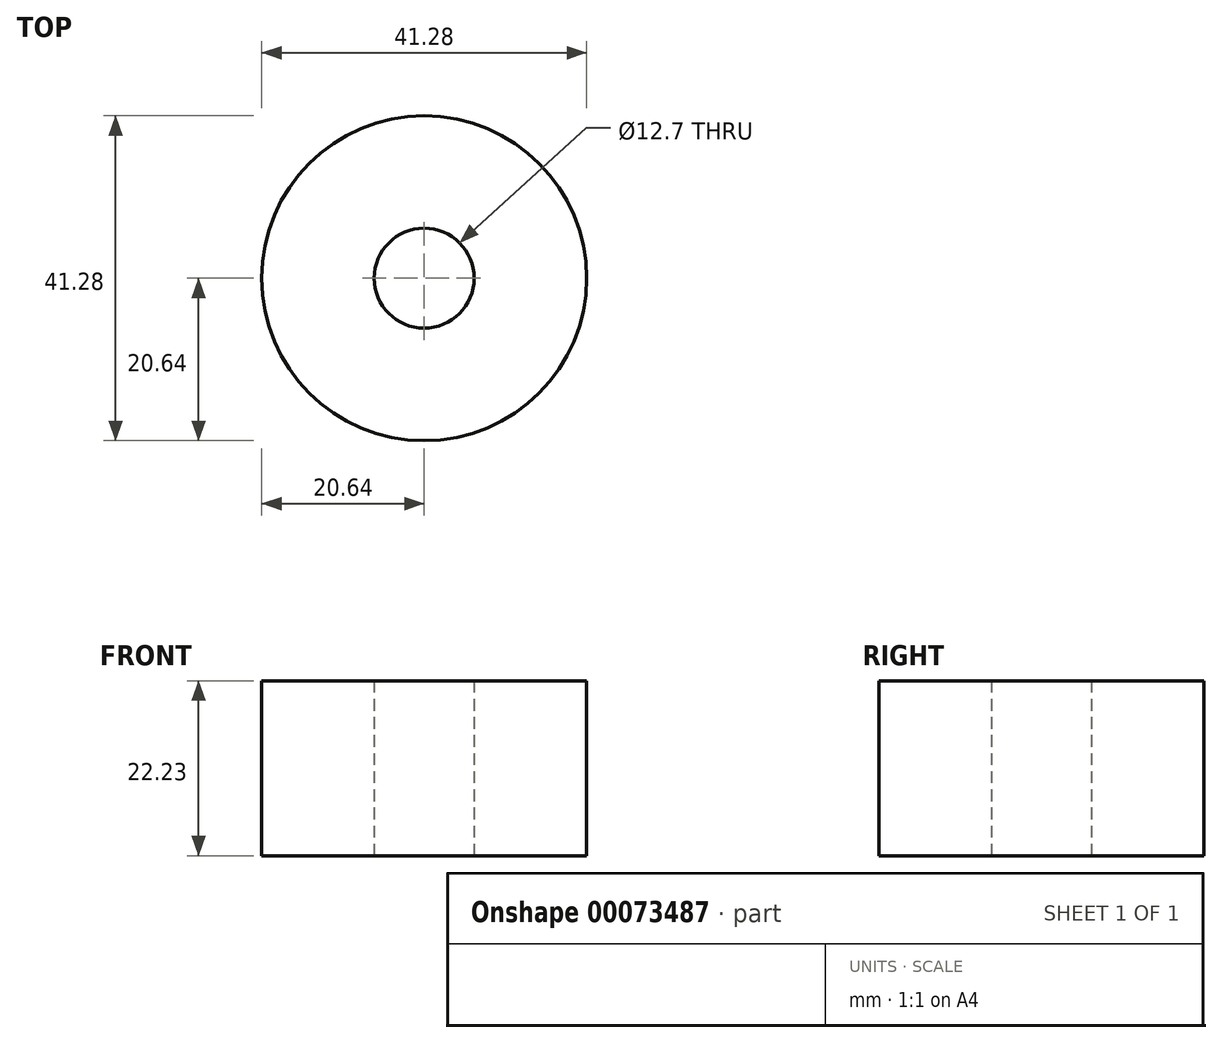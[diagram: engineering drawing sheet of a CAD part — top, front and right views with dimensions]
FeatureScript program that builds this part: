
annotation { "Feature Type Name" : "Feature", "Feature Type Description" : "" }
export const myFeature = defineFeature(function(context is Context, id is Id, definition is map)
    precondition{}
    {
        {
            var Q0;
            Q0=qCreatedBy(makeId("Top.planeOp"),FACE);
            var sketch = newSketch(context, id + "F0", { "sketchPlane" : qUnion([Q0])});
            skCircle(sketch, "E0", {"center": v(0, 0) * mm, "radius": 20.64 * mm});
            skCircle(sketch, "E1", {"center": v(0, 0) * mm, "radius": 6.35 * mm});
            skSolve(sketch);
        }
        {
            var Q0;
            Q0=makeQuery(id+"F0.imprint","IMPRINT",FACE,{"disambiguationData":[TD([[makeQuery(id+"F0.imprint","IMPRINT",EDGE,{"derivedFrom":sQuery(id+"F0.wireOp",EDGE,"E0")}),1.0]])]});
            extrude(context, id + "F1", {"entities" : qUnion([Q0]), "depth" : 22.22 * mm});
        }
    });
